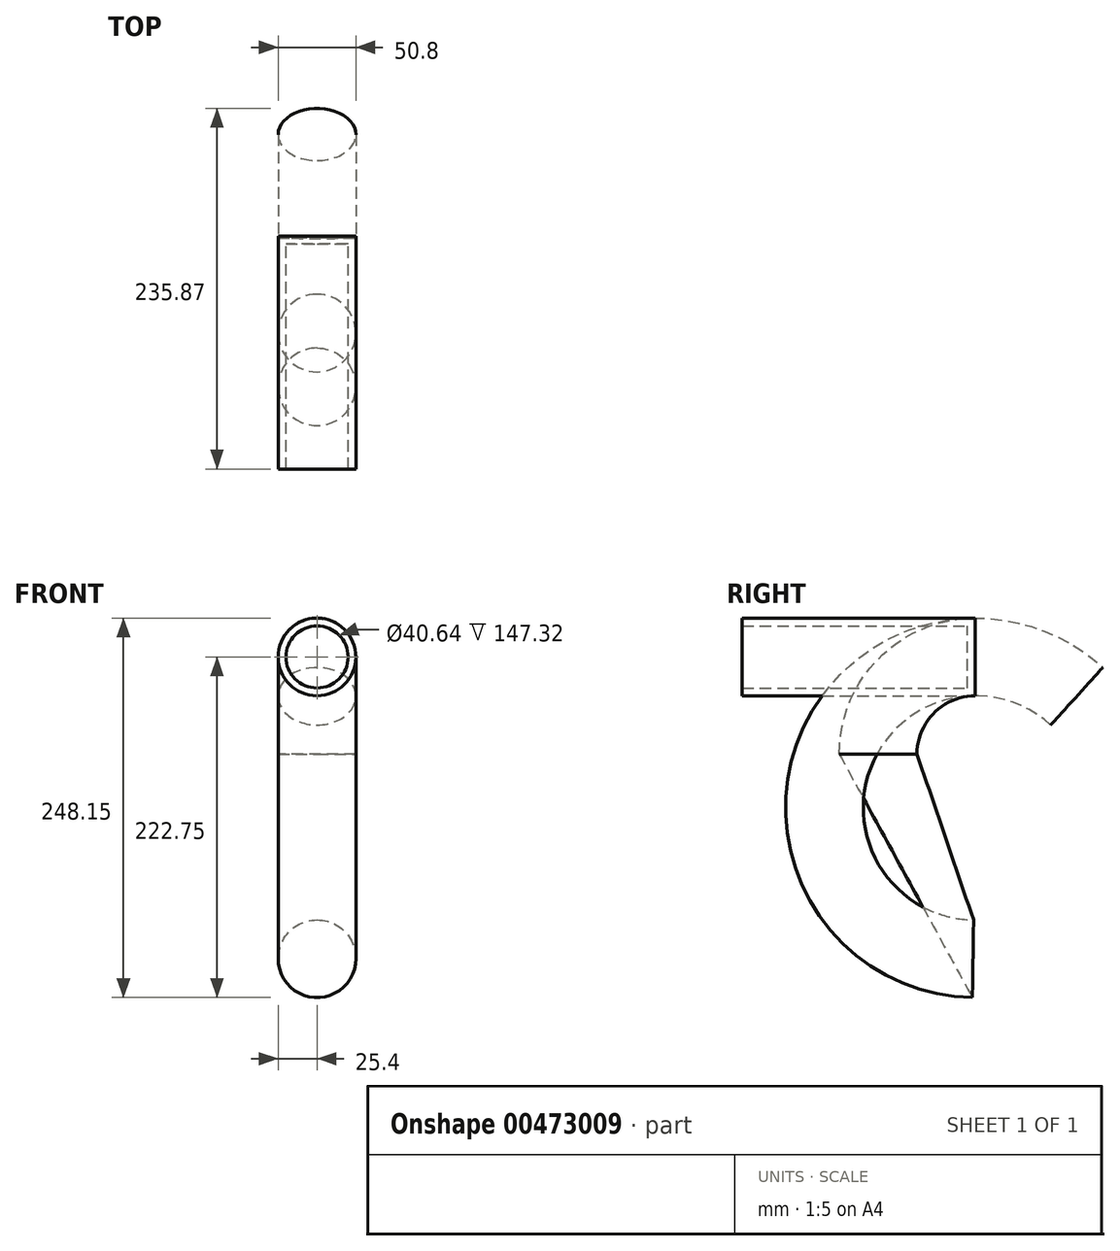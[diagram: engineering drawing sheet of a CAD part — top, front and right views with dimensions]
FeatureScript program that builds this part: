
annotation { "Feature Type Name" : "Feature", "Feature Type Description" : "" }
export const myFeature = defineFeature(function(context is Context, id is Id, definition is map)
    precondition{}
    {
        {
            var Q0;
            Q0=qCreatedBy(makeId("Front.planeOp"),FACE);
            var sketch = newSketch(context, id + "F0", { "sketchPlane" : qUnion([Q0])});
            skCircle(sketch, "E0", {"center": v(0, 0) * mm, "radius": 25.4 * mm});
            skLineSegment(sketch, "E1", {"start": v(0, -63.5) * mm, "end": v(76.2, -63.5) * mm});
            skSolve(sketch);
        }
        {
            var Q0;
            Q0 = qSketchRegion(id + "F0", true);
            extrude(context, id + "F1", {"entities" : qUnion([Q0]), "depth" : 152.4 * mm});
        }
        {
            var Q0;
            Q0=makeQuery(id+"F0.imprint","IMPRINT",FACE,{"disambiguationData":[TD([[makeQuery(id+"F0.imprint","IMPRINT",EDGE,{"derivedFrom":sQuery(id+"F0.wireOp",EDGE,"E0")}),1.0]])]});
            var Q1;
            Q1=sQuery(id+"F0.wireOp",EDGE,"E1");
            revolve(context, id + "F2", {"entities" : qUnion([Q0]), "axis" : qUnion([Q1]), "revolveType" : RevolveType.ONE_DIRECTION, "angle" : 90 * degree});
        }
        {
            var Q0;
            Q0=qCreatedBy(makeId("Right.planeOp"),FACE);
            var sketch = newSketch(context, id + "F3", { "sketchPlane" : qUnion([Q0])});
            skArc(sketch, "E2", {"start": v(-66.38, -171.69) * mm, "mid": v(91.78, -135) * mm, "end": v(1.59, -0.01) * mm});
            skSolve(sketch);
        }
        {
            var Q0;
            Q0=makeQuery(id+"F1.opExtrude","CAP_FACE",FACE,{"disambiguationData":[OSD([sQuery(id+"F0.wireOp",EDGE,"E0")])],"isStart":true});
            var Q1;
            Q1=makeQuery(id+"F1.opExtrude","CAP_EDGE",EDGE,{"disambiguationData":[OSD([sQuery(id+"F0.wireOp",EDGE,"E0")])],"isStart":true});
            var Q2;
            Q2=sQuery(id+"F3.wireOp",EDGE,"E2");
            sweep(context, id + "F4", {"profiles" : qUnion([Q0]), "surfaceProfiles" : qUnion([Q1]), "path" : qUnion([Q2])});
        }
        {
            var Q0;
            Q0=makeQuery(id+"F4.opSweep","CAP_FACE",FACE,{"disambiguationData":[OSD([sQuery(id+"F0.wireOp",EDGE,"E0"),sQuery(id+"F3.wireOp",VERTEX,"E2.start")])],"isStart":false});
            var Q1;
            Q1=makeQuery(id+"F2.opRevolve","CAP_FACE",FACE,{"disambiguationData":[OSD([sQuery(id+"F0.wireOp",EDGE,"E0")])],"isStart":false});
            loft(context, id + "F5", {"sheetProfilesArray" : [{ "sheetProfileEntities" : qUnion([Q0]) }, { "sheetProfileEntities" : qUnion([Q1]) }]});
        }
        {
            var Q0;
            Q0=makeQuery(id+"F1.opExtrude","CAP_FACE",FACE,{"disambiguationData":[OSD([sQuery(id+"F0.wireOp",EDGE,"E0")])],"isStart":false});
            shell(context, id + "F6", {"entities" : qUnion([Q0]), "thickness" : 5.08 * mm});
        }
    });
